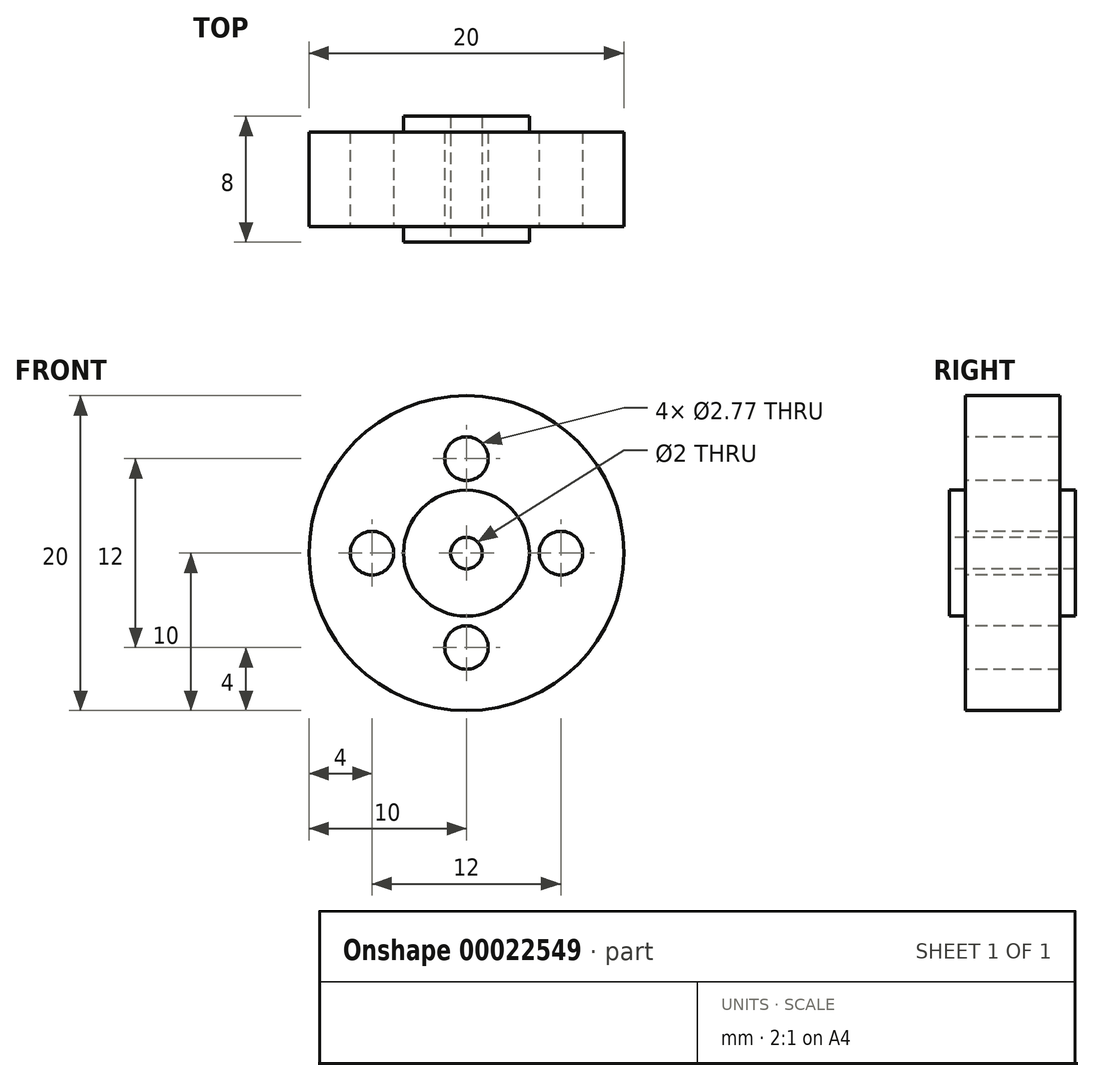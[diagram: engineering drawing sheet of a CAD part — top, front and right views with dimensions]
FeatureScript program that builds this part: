
annotation { "Feature Type Name" : "Feature", "Feature Type Description" : "" }
export const myFeature = defineFeature(function(context is Context, id is Id, definition is map)
    precondition{}
    {
        {
            var Q0;
            Q0=qCreatedBy(makeId("Front.planeOp"),FACE);
            var sketch = newSketch(context, id + "F0", { "sketchPlane" : qUnion([Q0])});
            skCircle(sketch, "E0", {"center": v(0, 0) * mm, "radius": 10 * mm});
            skSolve(sketch);
        }
        {
            var Q0;
            Q0=makeQuery(id+"F0.imprint","IMPRINT",FACE,{"disambiguationData":[TD([[makeQuery(id+"F0.imprint","IMPRINT",EDGE,{"derivedFrom":sQuery(id+"F0.wireOp",EDGE,"E0")}),1.0]])]});
            extrude(context, id + "F1", {"entities" : qUnion([Q0]), "depth" : 6 * mm});
        }
        {
            var Q0;
            Q0=makeQuery(id+"F1.opExtrude","CAP_FACE",FACE,{"disambiguationData":[OSD([sQuery(id+"F0.wireOp",EDGE,"E0")])],"isStart":false});
            var sketch = newSketch(context, id + "F2", { "sketchPlane" : qUnion([Q0])});
            skCircle(sketch, "E1", {"center": v(0, 0) * mm, "radius": 4 * mm});
            skSolve(sketch);
        }
        {
            var Q0;
            Q0=makeQuery(id+"F2.imprint","IMPRINT",FACE,{"disambiguationData":[TD([[makeQuery(id+"F2.imprint","IMPRINT",EDGE,{"derivedFrom":sQuery(id+"F2.wireOp",EDGE,"E1")}),1.0]])]});
            extrude(context, id + "F3", {"entities" : qUnion([Q0]), "operationType" : NewBodyOperationType.ADD, "depth" : 1 * mm});
        }
        {
            var Q0;
            Q0=makeQuery(id+"F3.opExtrude","CAP_FACE",FACE,{"disambiguationData":[OSD([sQuery(id+"F2.wireOp",EDGE,"E1")])],"isStart":false});
            var sketch = newSketch(context, id + "F4", { "sketchPlane" : qUnion([Q0])});
            skCircle(sketch, "E2", {"center": v(0, 0) * mm, "radius": 1 * mm});
            skSolve(sketch);
        }
        {
            var Q0;
            Q0=makeQuery(id+"F4.imprint","IMPRINT",FACE,{"disambiguationData":[TD([[makeQuery(id+"F4.imprint","IMPRINT",EDGE,{"derivedFrom":sQuery(id+"F4.wireOp",EDGE,"E2")}),1.0]])]});
            extrude(context, id + "F5", {"entities" : qUnion([Q0]), "operationType" : NewBodyOperationType.REMOVE, "oppositeDirection" : true, "depth" : 25.4 * mm});
        }
        {
            var Q0;
            Q0=makeQuery(id+"F1.opExtrude","CAP_FACE",FACE,{"disambiguationData":[OSD([sQuery(id+"F0.wireOp",EDGE,"E0")])],"isStart":true});
            var sketch = newSketch(context, id + "F6", { "sketchPlane" : qUnion([Q0])});
            skCircle(sketch, "E3", {"center": v(0, 0) * mm, "radius": 4 * mm});
            skSolve(sketch);
        }
        {
            var Q0;
            Q0=makeQuery(id+"F6.imprint","IMPRINT",FACE,{"disambiguationData":[TD([[makeQuery(id+"F6.imprint","IMPRINT",EDGE,{"derivedFrom":sQuery(id+"F6.wireOp",EDGE,"E3")}),1.0]])]});
            extrude(context, id + "F7", {"entities" : qUnion([Q0]), "operationType" : NewBodyOperationType.ADD, "depth" : 1 * mm});
        }
        {
            var Q0;
            Q0=makeQuery(id+"F1.opExtrude","CAP_FACE",FACE,{"disambiguationData":[OSD([sQuery(id+"F0.wireOp",EDGE,"E0")])],"isStart":false});
            var sketch = newSketch(context, id + "F8", { "sketchPlane" : qUnion([Q0])});
            skCircle(sketch, "E4", {"center": v(6, 0) * mm, "radius": 1.38 * mm});
            skCircle(sketch, "E5.1.0", {"center": v(0, 6) * mm, "radius": 1.38 * mm});
            skCircle(sketch, "E5.2.0", {"center": v(-6, 0) * mm, "radius": 1.38 * mm});
            skCircle(sketch, "E5.3.0", {"center": v(0, -6) * mm, "radius": 1.38 * mm});
            skPoint(sketch, "E5.center", {"position": v(0, 0) * mm});
            skLineSegment(sketch, "E6", {"start": v(0, 0) * mm, "end": v(-6, 0) * mm});
            skSolve(sketch);
        }
        {
            var Q0;
            Q0=makeQuery(id+"F8.imprint","IMPRINT",FACE,{"disambiguationData":[TD([[makeQuery(id+"F8.imprint","IMPRINT",EDGE,{"derivedFrom":sQuery(id+"F8.wireOp",EDGE,"E5.4.0")}),1.0]])]});
            var Q1;
            Q1=makeQuery(id+"F8.imprint","IMPRINT",FACE,{"disambiguationData":[TD([[makeQuery(id+"F8.imprint","IMPRINT",EDGE,{"derivedFrom":sQuery(id+"F8.wireOp",EDGE,"E5.5.0")}),1.0]])]});
            var Q2;
            Q2=makeQuery(id+"F8.imprint","IMPRINT",FACE,{"disambiguationData":[TD([[makeQuery(id+"F8.imprint","IMPRINT",EDGE,{"derivedFrom":sQuery(id+"F8.wireOp",EDGE,"E5.3.0")}),1.0]])]});
            var Q3;
            Q3=makeQuery(id+"F8.imprint","IMPRINT",FACE,{"disambiguationData":[TD([[makeQuery(id+"F8.imprint","IMPRINT",EDGE,{"derivedFrom":sQuery(id+"F8.wireOp",EDGE,"E5.2.0")}),1.0]])]});
            var Q4;
            Q4=makeQuery(id+"F8.imprint","IMPRINT",FACE,{"disambiguationData":[TD([[makeQuery(id+"F8.imprint","IMPRINT",EDGE,{"derivedFrom":sQuery(id+"F8.wireOp",EDGE,"E5.1.0")}),1.0]])]});
            var Q5;
            Q5=makeQuery(id+"F8.imprint","IMPRINT",FACE,{"disambiguationData":[TD([[makeQuery(id+"F8.imprint","IMPRINT",EDGE,{"derivedFrom":sQuery(id+"F8.wireOp",EDGE,"E4")}),1.0]])]});
            var Q6;
            Q6=sQuery(id+"F8.wireOp",EDGE,"E5.2.0");
            var Q7;
            Q7=sQuery(id+"F8.wireOp",EDGE,"E5.3.0");
            var Q8;
            Q8=sQuery(id+"F8.wireOp",EDGE,"E5.4.0");
            var Q9;
            Q9=sQuery(id+"F8.wireOp",EDGE,"E5.5.0");
            var Q10;
            Q10=sQuery(id+"F8.wireOp",EDGE,"E4");
            var Q11;
            Q11=sQuery(id+"F8.wireOp",EDGE,"E5.1.0");
            extrude(context, id + "F9", {"entities" : qUnion([Q0, Q1, Q2, Q3, Q4, Q5]), "operationType" : NewBodyOperationType.REMOVE, "surfaceEntities" : qUnion([Q6, Q7, Q8, Q9, Q10, Q11]), "endBound" : BoundingType.THROUGH_ALL, "oppositeDirection" : true, "depth" : 25.4 * mm});
        }
        {
            var Q0;
            Q0=makeQuery(id+"F1.opExtrude","SWEPT_BODY",BODY,{"disambiguationData":[OSD([sQuery(id+"F0.wireOp",EDGE,"E0")])]});
            transform(context, id + "F10", {"entities" : qUnion([Q0]), "transformType" : TransformType.TRANSLATION_3D, "dx" : 0 * mm, "dy" : 0 * mm, "dz" : 0 * mm, "makeCopy" : true});
        }
        {
            var Q0;
            Q0=makeQuery(id+"F10.opPattern","COPY",BODY,{"derivedFrom":makeQuery(id+"F1.opExtrude","SWEPT_BODY",BODY,{"disambiguationData":[OSD([sQuery(id+"F0.wireOp",EDGE,"E0")])]}),"instanceName":"1"});
            deleteBodies(context, id + "F11", {"entities" : qUnion([Q0])});
        }
    });
